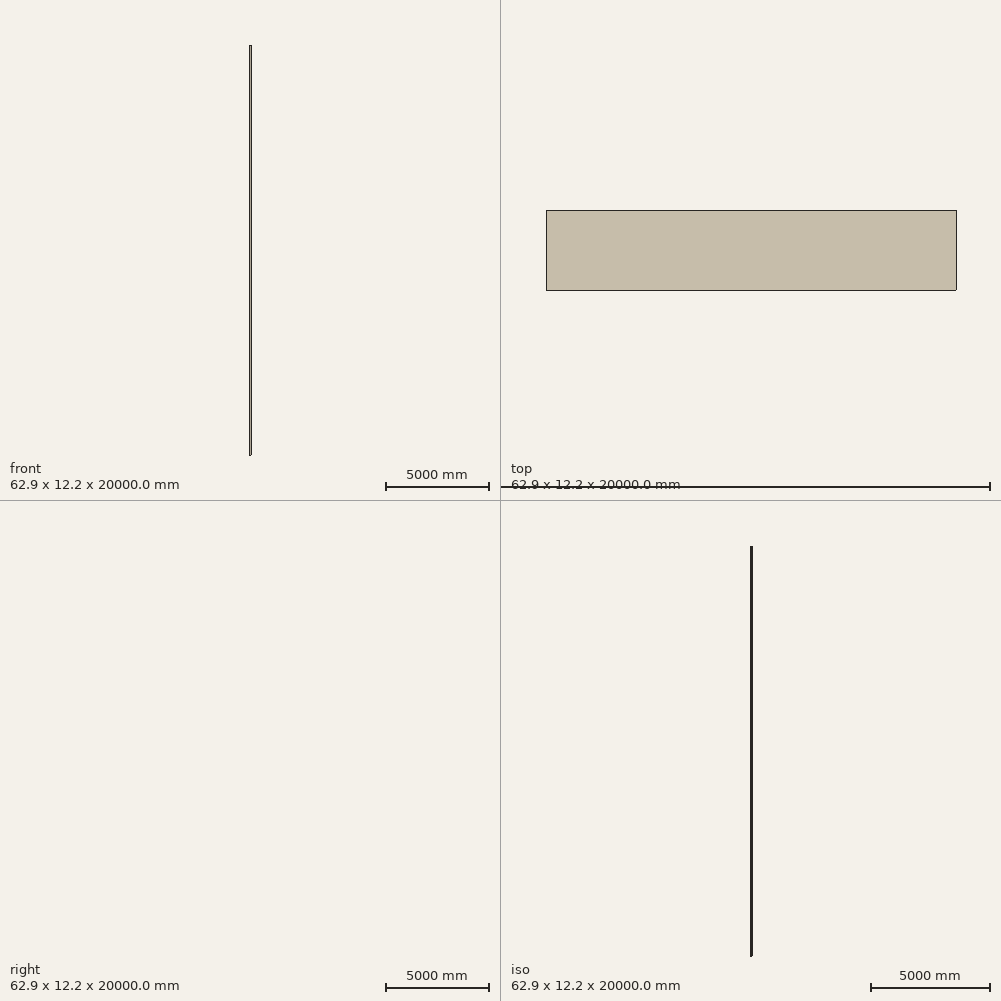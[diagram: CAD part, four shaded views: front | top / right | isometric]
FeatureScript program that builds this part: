
annotation { "Feature Type Name" : "Feature", "Feature Type Description" : "" }
export const myFeature = defineFeature(function(context is Context, id is Id, definition is map)
    precondition{}
    {
        {
            var Q0;
            Q0=qCreatedBy(makeId("Top.planeOp"),FACE);
            var sketch = newSketch(context, id + "F0", { "sketchPlane" : qUnion([Q0])});
            skLineSegment(sketch, "E0.bottom", {"start": v(-29.9, 6.82) * mm, "end": v(33, 6.82) * mm});
            skLineSegment(sketch, "E0.top", {"start": v(-29.9, -5.38) * mm, "end": v(33, -5.38) * mm});
            skLineSegment(sketch, "E0.left", {"start": v(-29.9, 6.82) * mm, "end": v(-29.9, -5.38) * mm});
            skLineSegment(sketch, "E0.right", {"start": v(33, 6.82) * mm, "end": v(33, -5.38) * mm});
            skSolve(sketch);
        }
        {
            var Q0;
            Q0=makeQuery(id+"F0.imprint","IMPRINT",FACE,{"disambiguationData":[TD([[makeQuery(id+"F0.imprint","IMPRINT",EDGE,{"derivedFrom":sQuery(id+"F0.wireOp",EDGE,"E0.bottom")}),-1.0]])]});
            extrude(context, id + "F1", {"entities" : qUnion([Q0]), "depth" : 20000 * mm});
        }
    });
